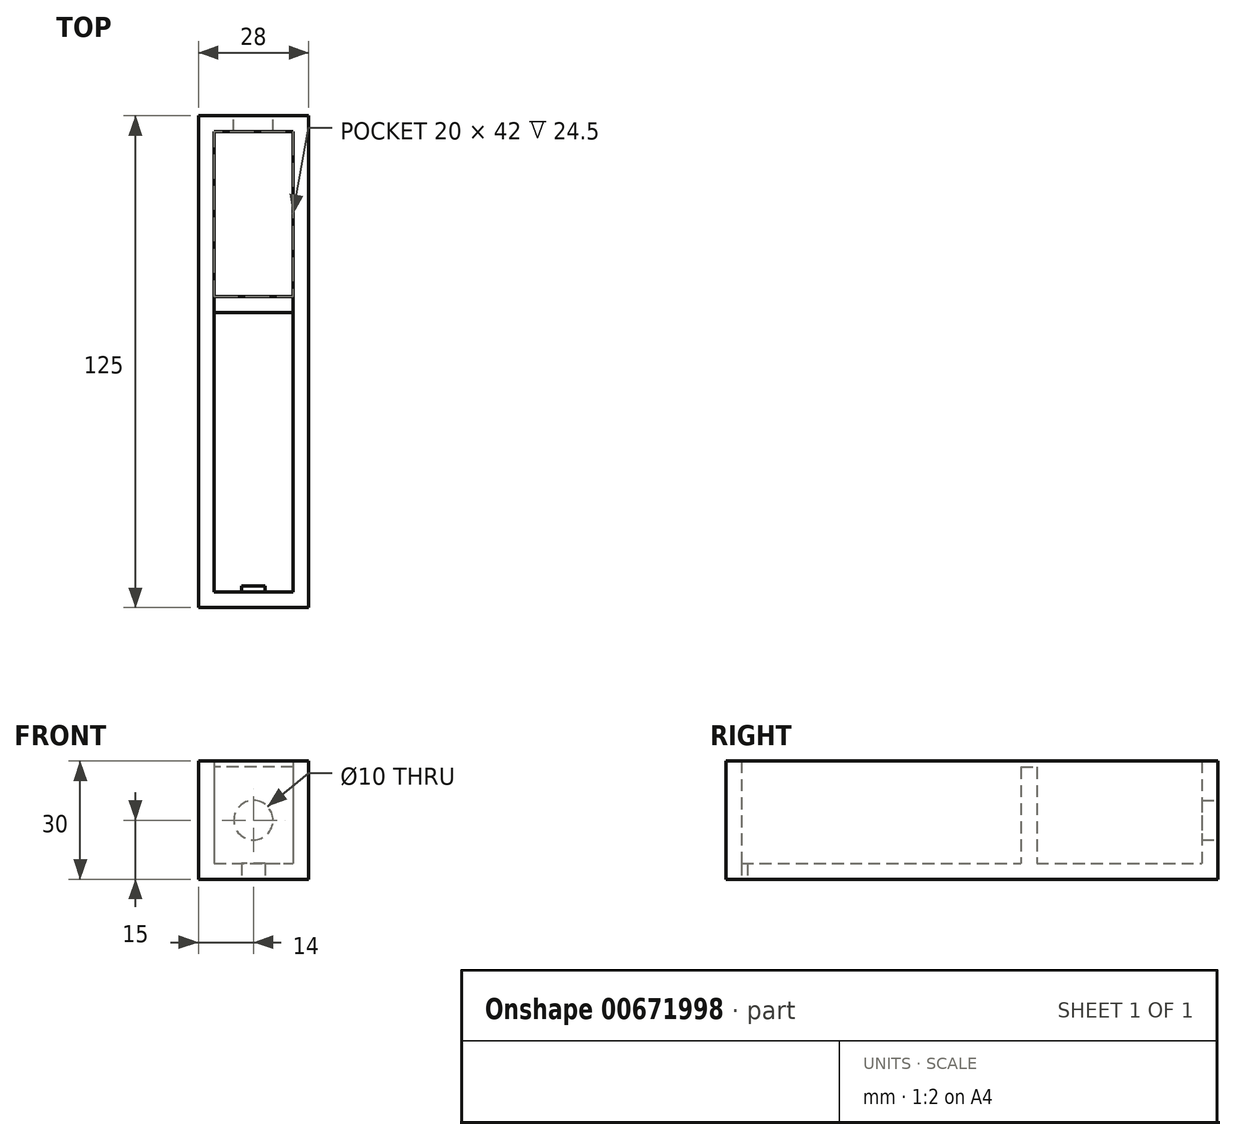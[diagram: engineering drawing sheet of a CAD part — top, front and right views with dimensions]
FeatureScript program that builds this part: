
annotation { "Feature Type Name" : "Feature", "Feature Type Description" : "" }
export const myFeature = defineFeature(function(context is Context, id is Id, definition is map)
    precondition{}
    {
        {
            var Q0;
            Q0=qCreatedBy(makeId("Top.planeOp"),FACE);
            var sketch = newSketch(context, id + "F0", { "sketchPlane" : qUnion([Q0])});
            skLineSegment(sketch, "E0.bottom", {"start": v(0, 0) * mm, "end": v(28, 0) * mm});
            skLineSegment(sketch, "E0.top", {"start": v(0, 79) * mm, "end": v(28, 79) * mm});
            skLineSegment(sketch, "E0.left", {"start": v(0, 0) * mm, "end": v(0, 79) * mm});
            skLineSegment(sketch, "E0.right", {"start": v(28, 0) * mm, "end": v(28, 79) * mm});
            skLineSegment(sketch, "E1.0", {"start": v(24, 4) * mm, "end": v(24, 75) * mm});
            skLineSegment(sketch, "E1.1", {"start": v(4, 4) * mm, "end": v(24, 4) * mm});
            skLineSegment(sketch, "E1.2", {"start": v(4, 4) * mm, "end": v(4, 75) * mm});
            skLineSegment(sketch, "E1.3", {"start": v(4, 75) * mm, "end": v(24, 75) * mm});
            skLineSegment(sketch, "E2.bottom", {"start": v(14, 4) * mm, "end": v(17, 4) * mm});
            skLineSegment(sketch, "E2.top", {"start": v(14, 5.5) * mm, "end": v(17, 5.5) * mm});
            skLineSegment(sketch, "E2.right", {"start": v(17, 4) * mm, "end": v(17, 5.5) * mm});
            skLineSegment(sketch, "E3.bottom", {"start": v(14, 5.5) * mm, "end": v(11, 5.5) * mm});
            skLineSegment(sketch, "E3.top", {"start": v(14, 4) * mm, "end": v(11, 4) * mm});
            skLineSegment(sketch, "E3.right", {"start": v(11, 5.5) * mm, "end": v(11, 4) * mm});
            skSolve(sketch);
        }
        {
            var Q0;
            Q0=makeQuery(id+"F0.imprint","IMPRINT",FACE,{"disambiguationData":[TD([[makeQuery(id+"F0.imprint","IMPRINT",EDGE,{"derivedFrom":sQuery(id+"F0.wireOp",EDGE,"E1.0")}),1.0]])]});
            extrude(context, id + "F1", {"entities" : qUnion([Q0]), "depth" : 4 * mm, "offsetDistance" : 25 * mm});
        }
        {
            var Q0;
            Q0=makeQuery(id+"F0.imprint","IMPRINT",FACE,{"disambiguationData":[TD([[makeQuery(id+"F0.imprint","IMPRINT",EDGE,{"derivedFrom":sQuery(id+"F0.wireOp",EDGE,"E0.bottom")}),1.0]])]});
            extrude(context, id + "F2", {"entities" : qUnion([Q0]), "operationType" : NewBodyOperationType.ADD, "depth" : 30 * mm, "offsetDistance" : 25 * mm});
        }
        {
            var Q0;
            Q0=makeQuery(id+"F2.opExtrude","SWEPT_FACE",FACE,{"disambiguationData":[OSD([sQuery(id+"F0.wireOp",EDGE,"E0.top")])]});
            var sketch = newSketch(context, id + "F3", { "sketchPlane" : qUnion([Q0])});
            skLineSegment(sketch, "E4.bottom", {"start": v(-14, 30) * mm, "end": v(-4, 30) * mm});
            skLineSegment(sketch, "E4.top", {"start": v(-14, 28.5) * mm, "end": v(-4, 28.5) * mm});
            skLineSegment(sketch, "E4.left", {"start": v(-14, 30) * mm, "end": v(-14, 28.5) * mm});
            skLineSegment(sketch, "E4.right", {"start": v(-4, 30) * mm, "end": v(-4, 28.5) * mm});
            skLineSegment(sketch, "E5.MirrorCS", {"start": v(-24, 30) * mm, "end": v(-24, 28.5) * mm});
            skLineSegment(sketch, "E6.MirrorCS", {"start": v(-14, 28.5) * mm, "end": v(-24, 28.5) * mm});
            skLineSegment(sketch, "E7.MirrorCS", {"start": v(-14, 30) * mm, "end": v(-24, 30) * mm});
            skSolve(sketch);
        }
        {
            var Q0;
            Q0=makeQuery(id+"F3.imprint","IMPRINT",FACE,{"disambiguationData":[TD([[makeQuery(id+"F3.imprint","IMPRINT",EDGE,{"derivedFrom":sQuery(id+"F3.wireOp",EDGE,"E4.bottom")}),1.0]])]});
            var Q1;
            Q1=makeQuery(id+"F3.imprint","IMPRINT",FACE,{"disambiguationData":[TD([[makeQuery(id+"F3.imprint","IMPRINT",EDGE,{"derivedFrom":sQuery(id+"F3.wireOp",EDGE,"E4.left")}),-1.0]])]});
            var Q2;
            Q2=makeQuery(id+"F2.opExtrude","SWEPT_FACE",FACE,{"disambiguationData":[OSD([sQuery(id+"F0.wireOp",EDGE,"E1.3")])]});
            extrude(context, id + "F4", {"entities" : qUnion([Q0, Q1]), "operationType" : NewBodyOperationType.REMOVE, "endBound" : BoundingType.UP_TO_SURFACE, "oppositeDirection" : true, "depth" : 25 * mm, "endBoundEntityFace" : qUnion([Q2]), "offsetDistance" : 25 * mm});
        }
        {
            var Q0;
            Q0=qCreatedBy(makeId("Top.planeOp"),FACE);
            var sketch = newSketch(context, id + "F5", { "sketchPlane" : qUnion([Q0])});
            skLineSegment(sketch, "E8.0.0", {"start": v(28, 79) * mm, "end": v(24, 79) * mm});
            skLineSegment(sketch, "E8.0.1", {"start": v(24, 79) * mm, "end": v(24, 4) * mm});
            skLineSegment(sketch, "E8.0.2", {"start": v(24, 4) * mm, "end": v(4, 4) * mm});
            skLineSegment(sketch, "E8.0.3", {"start": v(4, 4) * mm, "end": v(4, 79) * mm});
            skLineSegment(sketch, "E8.0.4", {"start": v(4, 79) * mm, "end": v(0, 79) * mm});
            skLineSegment(sketch, "E8.0.5", {"start": v(0, 79) * mm, "end": v(0, 0) * mm});
            skLineSegment(sketch, "E8.0.6", {"start": v(0, 0) * mm, "end": v(28, 0) * mm});
            skLineSegment(sketch, "E8.0.7", {"start": v(28, 0) * mm, "end": v(28, 79) * mm});
            skLineSegment(sketch, "E9.bottom", {"start": v(0, 79) * mm, "end": v(28, 79) * mm});
            skLineSegment(sketch, "E9.top", {"start": v(0, 125) * mm, "end": v(28, 125) * mm});
            skLineSegment(sketch, "E9.left", {"start": v(0, 79) * mm, "end": v(0, 125) * mm});
            skLineSegment(sketch, "E9.right", {"start": v(28, 79) * mm, "end": v(28, 125) * mm});
            skLineSegment(sketch, "E10.0", {"start": v(24, 79) * mm, "end": v(24, 121) * mm});
            skLineSegment(sketch, "E10.1", {"start": v(4, 121) * mm, "end": v(24, 121) * mm});
            skLineSegment(sketch, "E10.2", {"start": v(4, 79) * mm, "end": v(4, 121) * mm});
            skSolve(sketch);
        }
        {
            var Q0;
            Q0=makeQuery(id+"F5.imprint","IMPRINT",FACE,{"disambiguationData":[TD([[makeQuery(id+"F5.imprint","IMPRINT",EDGE,{"derivedFrom":sQuery(id+"F5.wireOp",EDGE,"E9.top")}),-1.0]])]});
            extrude(context, id + "F6", {"entities" : qUnion([Q0]), "operationType" : NewBodyOperationType.ADD, "depth" : 30 * mm, "offsetDistance" : 25 * mm});
        }
        {
            var Q0;
            {var subQ0=sQuery(id+"F5.wireOp",EDGE,"E10.0");Q0=makeQuery(id+"F5.imprint","IMPRINT",FACE,{"disambiguationData":[TD([[makeQuery(id+"F5.imprint","IMPRINT",EDGE,{"derivedFrom":subQ0}),1.0]])]});}
            extrude(context, id + "F7", {"entities" : qUnion([Q0]), "operationType" : NewBodyOperationType.ADD, "depth" : 4 * mm, "offsetDistance" : 25 * mm});
        }
        {
            var Q0;
            Q0=makeQuery(id+"F6.opExtrude","SWEPT_FACE",FACE,{"disambiguationData":[OSD([sQuery(id+"F5.wireOp",EDGE,"E9.top")])]});
            var sketch = newSketch(context, id + "F8", { "sketchPlane" : qUnion([Q0])});
            skLineSegment(sketch, "E11.0.0", {"start": v(-28, 0) * mm, "end": v(0, 0) * mm});
            skLineSegment(sketch, "E11.0.1", {"start": v(0, 0) * mm, "end": v(0, 30) * mm});
            skLineSegment(sketch, "E11.0.2", {"start": v(0, 30) * mm, "end": v(-28, 30) * mm});
            skLineSegment(sketch, "E11.0.3", {"start": v(-28, 30) * mm, "end": v(-28, 0) * mm});
            skLineSegment(sketch, "E12", {"start": v(0, 15) * mm, "end": v(-28, 15) * mm, "construction": true});
            skCircle(sketch, "E13", {"center": v(-14, 15) * mm, "radius": 5 * mm});
            skSolve(sketch);
        }
        {
            var Q0;
            Q0=makeQuery(id+"F8.imprint","IMPRINT",FACE,{"disambiguationData":[TD([[makeQuery(id+"F8.imprint","IMPRINT",EDGE,{"derivedFrom":sQuery(id+"F8.wireOp",EDGE,"E13")}),1.0]])]});
            var Q1;
            Q1=makeQuery(id+"F6.opExtrude","SWEPT_FACE",FACE,{"disambiguationData":[OSD([sQuery(id+"F5.wireOp",EDGE,"E10.1")])]});
            extrude(context, id + "F9", {"entities" : qUnion([Q0]), "operationType" : NewBodyOperationType.REMOVE, "endBound" : BoundingType.UP_TO_SURFACE, "oppositeDirection" : true, "depth" : 25 * mm, "endBoundEntityFace" : qUnion([Q1]), "offsetDistance" : 25 * mm});
        }
    });
